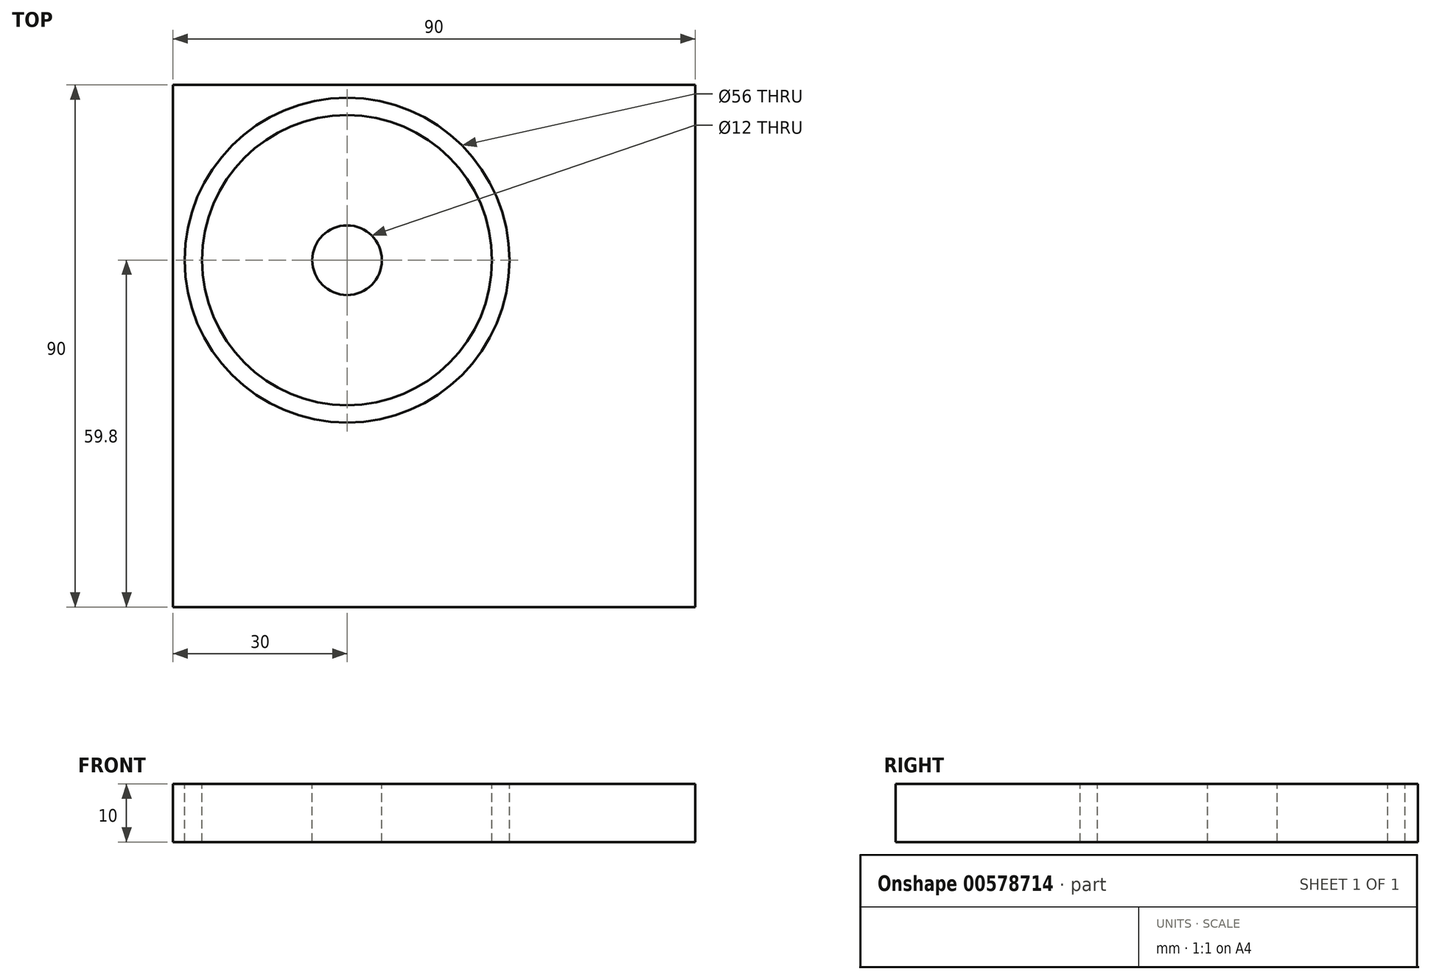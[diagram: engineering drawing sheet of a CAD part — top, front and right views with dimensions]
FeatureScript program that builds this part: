
annotation { "Feature Type Name" : "Feature", "Feature Type Description" : "" }
export const myFeature = defineFeature(function(context is Context, id is Id, definition is map)
    precondition{}
    {
        {
            var Q0;
            Q0=qCreatedBy(makeId("Top.planeOp"),FACE);
            var sketch = newSketch(context, id + "F0", { "sketchPlane" : qUnion([Q0])});
            skLineSegment(sketch, "E0.bottom", {"start": v(45, 45) * mm, "end": v(-45, 45) * mm});
            skLineSegment(sketch, "E0.top", {"start": v(45, -45) * mm, "end": v(-45, -45) * mm});
            skLineSegment(sketch, "E0.left", {"start": v(45, 45) * mm, "end": v(45, -45) * mm});
            skLineSegment(sketch, "E0.right", {"start": v(-45, 45) * mm, "end": v(-45, -45) * mm});
            skPoint(sketch, "E0.middle", {"position": v(0, 0) * mm});
            skSolve(sketch);
        }
        {
            var Q0;
            Q0 = qSketchRegion(id + "F0", true);
            extrude(context, id + "F1", {"entities" : qUnion([Q0]), "depth" : 10 * mm, "offsetDistance" : 25 * mm});
        }
        {
            var Q0;
            Q0=makeQuery(id+"F1.opExtrude","CAP_FACE",FACE,{"disambiguationData":[OSD([sQuery(id+"F0.wireOp",EDGE,"E0.bottom"),sQuery(id+"F0.wireOp",EDGE,"E0.top"),sQuery(id+"F0.wireOp",EDGE,"E0.left"),sQuery(id+"F0.wireOp",EDGE,"E0.right")])],"isStart":false});
            var sketch = newSketch(context, id + "F2", { "sketchPlane" : qUnion([Q0])});
            skLineSegment(sketch, "E1", {"start": v(-15, 45.45) * mm, "end": v(-15, -15.85) * mm, "construction": true});
            skLineSegment(sketch, "E2", {"start": v(-50.57, 15) * mm, "end": v(22.1, 15) * mm, "construction": true});
            skPoint(sketch, "E3", {"position": v(-15, 15) * mm});
            skPoint(sketch, "E3.positionSnap0", {"position": v(-15, 14.8) * mm});
            skSolve(sketch);
        }
        {
            var Q0;
            Q0=sQuery(id+"F2.wireOp",VERTEX,"E3.positionSnap0");
            var Q1;
            Q1=makeQuery(id+"F1.opExtrude","SWEPT_BODY",BODY,{"disambiguationData":[OSD([sQuery(id+"F0.wireOp",EDGE,"E0.bottom"),sQuery(id+"F0.wireOp",EDGE,"E0.top"),sQuery(id+"F0.wireOp",EDGE,"E0.left"),sQuery(id+"F0.wireOp",EDGE,"E0.right")])]});
            hole(context, id + "F3", {"style" : HoleStyle.SIMPLE, "endStyle" : HoleEndStyle.THROUGH, "holeDiameter" : 12 * mm, "isTappedThrough" : true, "tappedDepth" : 12 * mm, "tapClearance" : 3, "locations" : qUnion([Q0]), "scope" : qUnion([Q1])});
        }
        {
            var Q0;
            Q0=makeQuery(id+"F1.opExtrude","CAP_FACE",FACE,{"disambiguationData":[OSD([sQuery(id+"F0.wireOp",EDGE,"E0.bottom"),sQuery(id+"F0.wireOp",EDGE,"E0.top"),sQuery(id+"F0.wireOp",EDGE,"E0.left"),sQuery(id+"F0.wireOp",EDGE,"E0.right")])],"isStart":false});
            var sketch = newSketch(context, id + "F4", { "sketchPlane" : qUnion([Q0])});
            skCircle(sketch, "E4", {"center": v(-15, 14.8) * mm, "radius": 28 * mm});
            skCircle(sketch, "E5", {"center": v(-15, 14.8) * mm, "radius": 25 * mm});
            skSolve(sketch);
        }
        {
            var Q0;
            Q0 = qSketchRegion(id + "F4", true);
            var Q1;
            Q1=makeQuery(id+"F4.imprint","IMPRINT",FACE,{"disambiguationData":[TD([[makeQuery(id+"F4.imprint","IMPRINT",EDGE,{"derivedFrom":sQuery(id+"F4.wireOp",EDGE,"E4")}),1.0]])]});
            extrude(context, id + "F5", {"entities" : qUnion([Q0, Q1]), "operationType" : NewBodyOperationType.REMOVE, "endBound" : BoundingType.THROUGH_ALL, "oppositeDirection" : true, "depth" : 25 * mm, "offsetDistance" : 25 * mm});
        }
    });
